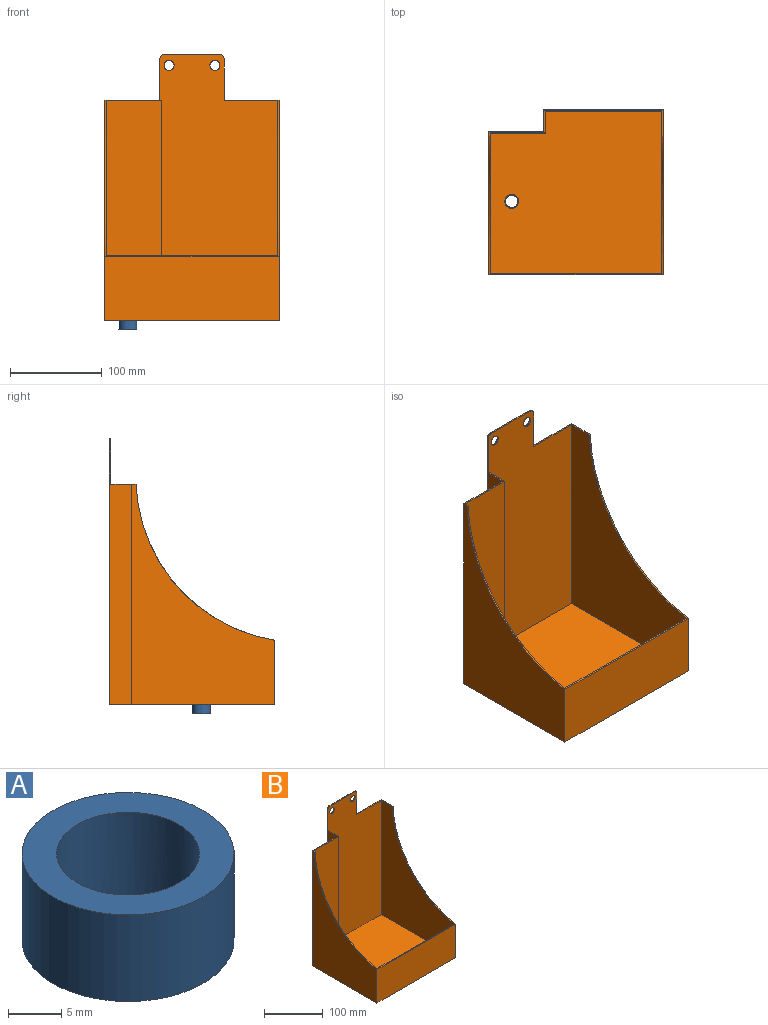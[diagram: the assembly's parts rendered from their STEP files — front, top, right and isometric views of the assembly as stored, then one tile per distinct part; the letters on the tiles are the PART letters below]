
ASSEMBLY  parts=2 mates=1
PART A: 4 faces, bbox 20x20x10 mm
  f0: cylinder r=10mm len=20mm, axis (0,0,-1), area 628.3mm2, adj f1,f2
  f1: plane 20x20mm, normal (0,0,1), area 171.2mm2, adj f0,f3
  f2: plane 20x20mm, normal (0,0,-1), area 171.2mm2, adj f0,f3
  f3: cylinder r=6.75mm len=13.49mm, axis (0,0,-1), area 423.9mm2, adj f1,f2
PART B: 24 faces, bbox 190x180x290 mm
  f0: plane 60x29mm, normal (0,0,1), area 139.8mm2, adj f2,f4,f8,f11,f15,f17
  f1: plane 61.6x27.4mm, normal (0,0,1), area 139.8mm2, adj f2,f5,f6,f7,f11,f12,f13,f14
  f2: cylinder r=180mm len=190mm, axis (-1,0,0), area 1090.6mm2, adj f0,f1,f3,f7,f8,f10,f14,f15
  f3: plane 190x70mm, normal (0,-1,0), area 13300mm2, adj f2,f7,f8,f9
  f4: plane 290x130mm, normal (0,1,0), area 34499.2mm2, adj f0,f5,f8,f9,f17,f18,f19,f20
  f5: plane 285x24mm, normal (-1,0,0), area 5832mm2, adj f1,f4,f6,f9,f11,f19
  f6: plane 240x60mm, normal (0,1,0), area 14400mm2, adj f1,f5,f7,f9
  f7: plane 240x156mm, normal (-1,0,0), area 18321.1mm2, adj f1,f2,f3,f6,f9
  f8: plane 240x180mm, normal (1,0,0), area 24081.1mm2, adj f0,f2,f3,f4,f9
  f9: plane 190x180mm, normal (0,0,-1), area 32583.3mm2, adj f3,f4,f5,f6,f7,f8,f23
  f10: plane 186.8x68.67mm, normal (0,1,0), area 12827mm2, adj f2,f14,f15,f16
  f11: plane 288.4x128.4mm, normal (0,-1,0), area 33528.3mm2, adj f0,f1,f5,f12,f15,f16,f17,f18
  f12: plane 238.4x24mm, normal (1,0,0), area 5721.6mm2, adj f1,f11,f13,f16
  f13: plane 238.4x60mm, normal (0,-1,0), area 14304mm2, adj f1,f12,f14,f16
  f14: plane 238.4x152.8mm, normal (1,0,0), area 17580.4mm2, adj f1,f2,f10,f13,f16
  f15: plane 238.4x176.8mm, normal (-1,0,0), area 23302mm2, adj f0,f2,f10,f11,f16
  f16: plane 186.8x176.8mm, normal (0,0,1), area 31409.5mm2, adj f10,f11,f12,f13,f14,f15,f23
  f17: plane 45x1.6mm, normal (1,0,0), area 72mm2, adj f0,f4,f11,f20
  f18: plane 60x1.6mm, normal (0,0,1), area 96mm2, adj f4,f11,f19,f20
  f19: cylinder r=5mm len=5mm, axis (0,1,0), area 12.6mm2, adj f4,f5,f11,f18
  f20: cylinder r=5mm len=5mm, axis (0,-1,0), area 12.6mm2, adj f4,f11,f17,f18
  f21: cylinder r=5.5mm len=11mm, axis (0,-1,0), area 55.3mm2, adj f4,f11
  f22: cylinder r=5.5mm len=11mm, axis (0,-1,0), area 55.3mm2, adj f4,f11
  f23: cylinder r=7.5mm len=15mm, axis (0,0,1), area 75.4mm2, adj f9,f16
PLACE A t=(-70,-100,-300)mm
PLACE B t=(0,0,-290)mm
MATE fastened A.f0 <-> B.f23  axis (0,0,-1) through (-70,-100,-290)mm
